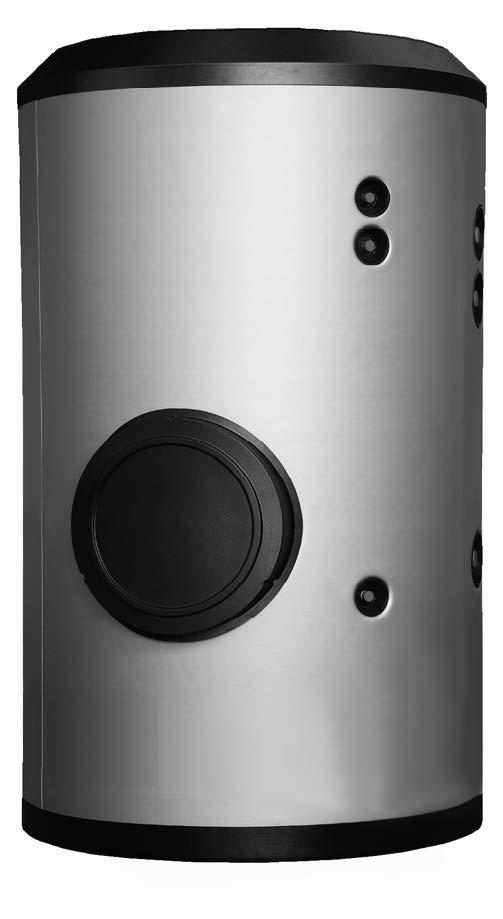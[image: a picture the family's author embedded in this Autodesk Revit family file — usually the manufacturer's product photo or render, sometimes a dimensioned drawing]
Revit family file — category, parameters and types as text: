
# Revit family: IMXV-3500SB_CC01835
name_source: partatom
category: Aparatos eléctricos
revit_build: Autodesk Revit 2016 (Build: 20150220_1215(x64)
units: mm (PartAtom-declared; Revit-internal decimal feet)

## family parameters
Compartido = No
Corte con vacíos al cargar = No
Número OmniClass = 23.80.00.00
Punto de cálculo de habitación = No
Se basa en plano de trabajo = No
Siempre vertical = Sí
Título OmniClass = Electric Power and Lighting

## types (1)
- Depósitos gran capacidad IMXV-SB
    Clase eficiencia energética = C
    Costo = 0 $
    Código de montaje = CC01835
    Descripción = DEPÓSITOS GRAN CAPACIDAD VITRIFICADOS ACERO INOX.
    Dimensiones = 1660 x 2580 mm
    Fabricante = SALVADOR ESCODA
    Imagen de tipo = RB-IMXV.jpg
    Modelo = IMXV 3500 SB
    Peso en vacío = 577 Kg
    Presión máx. circuito = 25 bar
    Presión máx. depósito = 8 bar
    Superfície intercambio = 8,4 m2
    Temperatura máx. ACS = 90 ºC
    Temperatura máx. circuito = 120 ºC
    URL = www.salvadorescoda.com
    Volúmen = 3500 l
